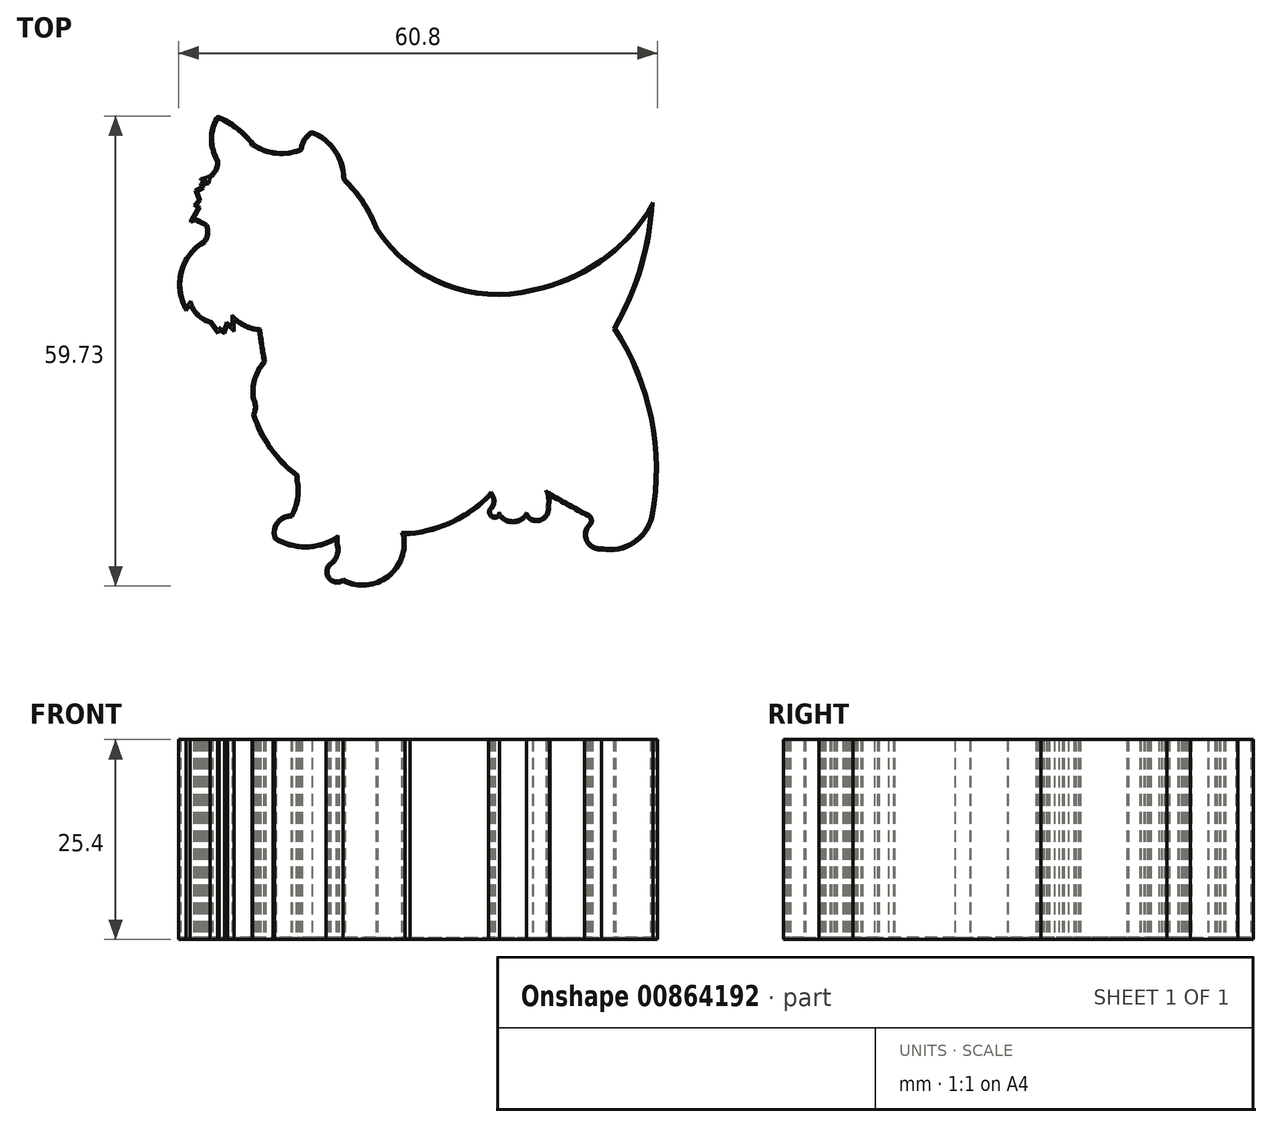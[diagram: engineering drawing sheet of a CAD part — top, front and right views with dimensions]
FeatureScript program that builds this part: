
annotation { "Feature Type Name" : "Feature", "Feature Type Description" : "" }
export const myFeature = defineFeature(function(context is Context, id is Id, definition is map)
    precondition{}
    {
        {
            var Q0;
            Q0=qCreatedBy(makeId("Top.planeOp"),FACE);
            var sketch = newSketch(context, id + "F0", { "sketchPlane" : qUnion([Q0])});
            skArc(sketch, "E0", {"start": v(-19.85, 25.73) * mm, "mid": v(-21.9, 27.84) * mm, "end": v(-24.45, 29.31) * mm});
            skArc(sketch, "E1", {"start": v(-24.45, 29.31) * mm, "mid": v(-25.34, 26.72) * mm, "end": v(-24.8, 24.03) * mm});
            skLineSegment(sketch, "E2", {"start": v(-24.8, 24.03) * mm, "end": v(-24.54, 23.52) * mm});
            skPoint(sketch, "E3.endSnap0", {"position": v(-25.09, 22.48) * mm});
            skPoint(sketch, "E4.endSnap0", {"position": v(-25.4, 22.2) * mm});
            skLineSegment(sketch, "E5", {"start": v(-26.63, 21.34) * mm, "end": v(-26.63, 21.16) * mm});
            skLineSegment(sketch, "E6", {"start": v(-26.63, 21.16) * mm, "end": v(-25.75, 21.16) * mm});
            skLineSegment(sketch, "E7", {"start": v(-25.75, 21.16) * mm, "end": v(-25.82, 20.92) * mm});
            skLineSegment(sketch, "E8", {"start": v(-25.82, 20.92) * mm, "end": v(-26.63, 20.73) * mm});
            skLineSegment(sketch, "E9", {"start": v(-26.63, 20.73) * mm, "end": v(-26.52, 20.3) * mm});
            skLineSegment(sketch, "E10", {"start": v(-26.52, 20.3) * mm, "end": v(-27.3, 19.83) * mm});
            skLineSegment(sketch, "E11", {"start": v(-27.3, 19.83) * mm, "end": v(-26.87, 18.62) * mm});
            skLineSegment(sketch, "E12", {"start": v(-26.87, 18.62) * mm, "end": v(-27.43, 17.97) * mm});
            skLineSegment(sketch, "E13", {"start": v(-27.43, 17.97) * mm, "end": v(-27, 17.6) * mm});
            skLineSegment(sketch, "E14", {"start": v(-27, 17.6) * mm, "end": v(-27.86, 15.99) * mm});
            skLineSegment(sketch, "E15", {"start": v(-27.86, 15.99) * mm, "end": v(-27.86, 15.84) * mm});
            skLineSegment(sketch, "E16", {"start": v(-27.86, 15.84) * mm, "end": v(-27.17, 15.99) * mm});
            skLineSegment(sketch, "E17", {"start": v(-27.08, 15.91) * mm, "end": v(-25.98, 15.36) * mm});
            skArc(sketch, "E18", {"start": v(-26.2, 13.43) * mm, "mid": v(-29.18, 9.47) * mm, "end": v(-28.45, 4.56) * mm});
            skLineSegment(sketch, "E19", {"start": v(-28.45, 4.56) * mm, "end": v(-27.93, 5.24) * mm});
            skArc(sketch, "E20", {"start": v(-27.93, 5.24) * mm, "mid": v(-26.92, 3.82) * mm, "end": v(-25.38, 2.98) * mm});
            skLineSegment(sketch, "E21", {"start": v(-25.38, 2.98) * mm, "end": v(-24.41, 1.64) * mm});
            skLineSegment(sketch, "E22", {"start": v(-24.41, 1.64) * mm, "end": v(-24.23, 2.05) * mm});
            skLineSegment(sketch, "E23", {"start": v(-24.23, 2.05) * mm, "end": v(-23.58, 1.64) * mm});
            skLineSegment(sketch, "E24", {"start": v(-23.58, 1.64) * mm, "end": v(-23.16, 2.72) * mm});
            skLineSegment(sketch, "E25", {"start": v(-23.16, 2.72) * mm, "end": v(-22.24, 1.85) * mm});
            skLineSegment(sketch, "E26", {"start": v(-22.34, 1.85) * mm, "end": v(-22.24, 1.85) * mm});
            skLineSegment(sketch, "E27", {"start": v(-22.34, 1.85) * mm, "end": v(-22.34, 2.67) * mm});
            skLineSegment(sketch, "E28", {"start": v(-22.34, 2.67) * mm, "end": v(-22.34, 3.4) * mm});
            skArc(sketch, "E29", {"start": v(-22.34, 3.4) * mm, "mid": v(-20.89, 2.48) * mm, "end": v(-19.22, 2.03) * mm});
            skArc(sketch, "E30", {"start": v(-19.22, 2.03) * mm, "mid": v(-18.94, 0.07) * mm, "end": v(-18.6, -1.88) * mm});
            skArc(sketch, "E31", {"start": v(-18.6, -1.88) * mm, "mid": v(-19.85, -4.14) * mm, "end": v(-19.98, -6.71) * mm});
            skArc(sketch, "E32", {"start": v(-19.98, -8.62) * mm, "mid": v(-19.76, -7.67) * mm, "end": v(-19.98, -6.71) * mm});
            skArc(sketch, "E33", {"start": v(-19.98, -8.62) * mm, "mid": v(-17.84, -12.96) * mm, "end": v(-14.44, -16.4) * mm});
            skArc(sketch, "E34", {"start": v(-15.12, -21.4) * mm, "mid": v(-14.4, -19.3) * mm, "end": v(-14.44, -17.07) * mm});
            skLineSegment(sketch, "E35", {"start": v(-14.44, -16.4) * mm, "end": v(-14.44, -17.07) * mm});
            skArc(sketch, "E36", {"start": v(-15.12, -21.4) * mm, "mid": v(-16.98, -22.37) * mm, "end": v(-17.2, -24.46) * mm});
            skArc(sketch, "E37", {"start": v(-17.2, -24.46) * mm, "mid": v(-13.29, -25.57) * mm, "end": v(-9.38, -24.46) * mm});
            skArc(sketch, "E38", {"start": v(-10.27, -27.6) * mm, "mid": v(-9.4, -26.52) * mm, "end": v(-9.38, -25.13) * mm});
            skArc(sketch, "E39", {"start": v(-10.27, -27.6) * mm, "mid": v(-10.37, -29.5) * mm, "end": v(-8.48, -29.83) * mm});
            skArc(sketch, "E40", {"start": v(-8.48, -29.83) * mm, "mid": v(-2.72, -29.3) * mm, "end": v(-0.73, -23.86) * mm});
            skArc(sketch, "E41", {"start": v(0, -23.86) * mm, "mid": v(5.6, -22.3) * mm, "end": v(10.31, -18.86) * mm});
            skArc(sketch, "E42", {"start": v(10.31, -20.35) * mm, "mid": v(10.53, -19.6) * mm, "end": v(10.31, -18.86) * mm});
            skArc(sketch, "E43", {"start": v(10.31, -20.35) * mm, "mid": v(10.17, -21.53) * mm, "end": v(11.35, -21.55) * mm});
            skArc(sketch, "E44", {"start": v(11.35, -21.55) * mm, "mid": v(13.07, -22.37) * mm, "end": v(14.78, -21.55) * mm});
            skArc(sketch, "E45", {"start": v(14.78, -21.55) * mm, "mid": v(16.71, -22.1) * mm, "end": v(17.7, -20.35) * mm});
            skArc(sketch, "E46", {"start": v(17.7, -20.35) * mm, "mid": v(17.77, -19.6) * mm, "end": v(17.7, -18.86) * mm});
            skArc(sketch, "E47", {"start": v(17.7, -18.86) * mm, "mid": v(20.13, -20.25) * mm, "end": v(22.61, -21.55) * mm});
            skArc(sketch, "E48", {"start": v(22.61, -22.67) * mm, "mid": v(22.91, -22.1) * mm, "end": v(22.61, -21.55) * mm});
            skArc(sketch, "E49", {"start": v(22.61, -22.67) * mm, "mid": v(22.4, -24.82) * mm, "end": v(24.33, -25.8) * mm});
            skArc(sketch, "E50", {"start": v(24.33, -25.8) * mm, "mid": v(28.47, -25.02) * mm, "end": v(30.86, -21.55) * mm});
            skArc(sketch, "E51", {"start": v(30.86, -21.55) * mm, "mid": v(30.79, -9.16) * mm, "end": v(26.12, 2.33) * mm});
            skArc(sketch, "E52", {"start": v(26.12, 2.33) * mm, "mid": v(29.44, 10.03) * mm, "end": v(30.86, 18.3) * mm});
            skArc(sketch, "E53", {"start": v(15.57, 7.3) * mm, "mid": v(24.4, 11.15) * mm, "end": v(30.86, 18.3) * mm});
            skArc(sketch, "E54", {"start": v(-4.1, 15.01) * mm, "mid": v(4.5, 8) * mm, "end": v(15.57, 7.3) * mm});
            skArc(sketch, "E55", {"start": v(-4.1, 15.01) * mm, "mid": v(-5.85, 18.4) * mm, "end": v(-8.27, 21.31) * mm});
            skArc(sketch, "E56", {"start": v(-8.27, 21.31) * mm, "mid": v(-9.43, 24.97) * mm, "end": v(-12.44, 27.35) * mm});
            skArc(sketch, "E57", {"start": v(-12.44, 27.35) * mm, "mid": v(-13.46, 26.42) * mm, "end": v(-13.95, 25.13) * mm});
            skArc(sketch, "E58", {"start": v(-19.85, 25.73) * mm, "mid": v(-16.98, 24.7) * mm, "end": v(-13.95, 25.13) * mm});
            skPoint(sketch, "E3.end.orphan", {"position": v(-25.09, 22.1) * mm});
            skPoint(sketch, "E3.start.orphan", {"position": v(-25.38, 22.48) * mm});
            skPoint(sketch, "E59.start.orphan", {"position": v(-24.8, 22.48) * mm});
            skPoint(sketch, "E4.end.orphan", {"position": v(-25.4, 22) * mm});
            skPoint(sketch, "E60.end.orphan", {"position": v(-25.7, 22.28) * mm});
            skArc(sketch, "E61", {"start": v(-26.63, 21.34) * mm, "mid": v(-25.14, 22) * mm, "end": v(-24.54, 23.52) * mm});
            skArc(sketch, "E62", {"start": v(-26.2, 13.43) * mm, "mid": v(-25.83, 14.37) * mm, "end": v(-25.98, 15.36) * mm});
            skPoint(sketch, "E63.start.orphan", {"position": v(-26.48, 14.81) * mm});
            skPoint(sketch, "E64.start.orphan", {"position": v(-26.63, 14.55) * mm});
            skPoint(sketch, "E65.start.orphan", {"position": v(-26.48, 14.03) * mm});
            skLineSegment(sketch, "E66", {"start": v(-0.73, -23.86) * mm, "end": v(0, -23.86) * mm});
            skLineSegment(sketch, "E67", {"start": v(-9.38, -25.13) * mm, "end": v(-9.38, -24.46) * mm});
            skLineSegment(sketch, "E68", {"start": v(-27.08, 15.91) * mm, "end": v(-27.17, 15.99) * mm});
            skSolve(sketch);
        }
        {
            var Q0;
            Q0=makeQuery(id+"F0.imprint","IMPRINT",FACE,{"disambiguationData":[TD([[makeQuery(id+"F0.imprint","IMPRINT",EDGE,{"derivedFrom":sQuery(id+"F0.wireOp",EDGE,"E0")}),1.0]])]});
            extrude(context, id + "F1", {"entities" : qUnion([Q0]), "depth" : 25.4 * mm, "offsetDistance" : 25.4 * mm});
        }
        {
            var Q0;
            Q0=makeQuery(id+"F1.opExtrude","CAP_FACE",FACE,{"disambiguationData":[OSD([sQuery(id+"F0.wireOp",EDGE,"E0"),sQuery(id+"F0.wireOp",EDGE,"E1"),sQuery(id+"F0.wireOp",EDGE,"E2"),sQuery(id+"F0.wireOp",EDGE,"E5"),sQuery(id+"F0.wireOp",EDGE,"E6"),sQuery(id+"F0.wireOp",EDGE,"E7"),sQuery(id+"F0.wireOp",EDGE,"E8"),sQuery(id+"F0.wireOp",EDGE,"E9"),sQuery(id+"F0.wireOp",EDGE,"E10"),sQuery(id+"F0.wireOp",EDGE,"E11"),sQuery(id+"F0.wireOp",EDGE,"E12"),sQuery(id+"F0.wireOp",EDGE,"E13"),sQuery(id+"F0.wireOp",EDGE,"E14"),sQuery(id+"F0.wireOp",EDGE,"E15"),sQuery(id+"F0.wireOp",EDGE,"E16"),sQuery(id+"F0.wireOp",EDGE,"E17"),sQuery(id+"F0.wireOp",EDGE,"E18"),sQuery(id+"F0.wireOp",EDGE,"E19"),sQuery(id+"F0.wireOp",EDGE,"E20"),sQuery(id+"F0.wireOp",EDGE,"E21"),sQuery(id+"F0.wireOp",EDGE,"E22"),sQuery(id+"F0.wireOp",EDGE,"E23"),sQuery(id+"F0.wireOp",EDGE,"E24"),sQuery(id+"F0.wireOp",EDGE,"E25"),sQuery(id+"F0.wireOp",EDGE,"E27"),sQuery(id+"F0.wireOp",EDGE,"E28"),sQuery(id+"F0.wireOp",EDGE,"E29"),sQuery(id+"F0.wireOp",EDGE,"E30"),sQuery(id+"F0.wireOp",EDGE,"E31"),sQuery(id+"F0.wireOp",EDGE,"E32"),sQuery(id+"F0.wireOp",EDGE,"E33"),sQuery(id+"F0.wireOp",EDGE,"E34"),sQuery(id+"F0.wireOp",EDGE,"E35"),sQuery(id+"F0.wireOp",EDGE,"E36"),sQuery(id+"F0.wireOp",EDGE,"E37"),sQuery(id+"F0.wireOp",EDGE,"E38"),sQuery(id+"F0.wireOp",EDGE,"E39"),sQuery(id+"F0.wireOp",EDGE,"E40"),sQuery(id+"F0.wireOp",EDGE,"E41"),sQuery(id+"F0.wireOp",EDGE,"E42"),sQuery(id+"F0.wireOp",EDGE,"E43"),sQuery(id+"F0.wireOp",EDGE,"E44"),sQuery(id+"F0.wireOp",EDGE,"E45"),sQuery(id+"F0.wireOp",EDGE,"E46"),sQuery(id+"F0.wireOp",EDGE,"E47"),sQuery(id+"F0.wireOp",EDGE,"E48"),sQuery(id+"F0.wireOp",EDGE,"E49"),sQuery(id+"F0.wireOp",EDGE,"E50"),sQuery(id+"F0.wireOp",EDGE,"E51"),sQuery(id+"F0.wireOp",EDGE,"E52"),sQuery(id+"F0.wireOp",EDGE,"E53"),sQuery(id+"F0.wireOp",EDGE,"E54"),sQuery(id+"F0.wireOp",EDGE,"E55"),sQuery(id+"F0.wireOp",EDGE,"E56"),sQuery(id+"F0.wireOp",EDGE,"E57"),sQuery(id+"F0.wireOp",EDGE,"E58"),sQuery(id+"F0.wireOp",EDGE,"E61"),sQuery(id+"F0.wireOp",EDGE,"E62"),sQuery(id+"F0.wireOp",EDGE,"E66"),sQuery(id+"F0.wireOp",EDGE,"E67"),sQuery(id+"F0.wireOp",EDGE,"E68")])],"isStart":false});
            shell(context, id + "F2", {"entities" : qUnion([Q0]), "thickness" : 0.25 * mm});
        }
    });
